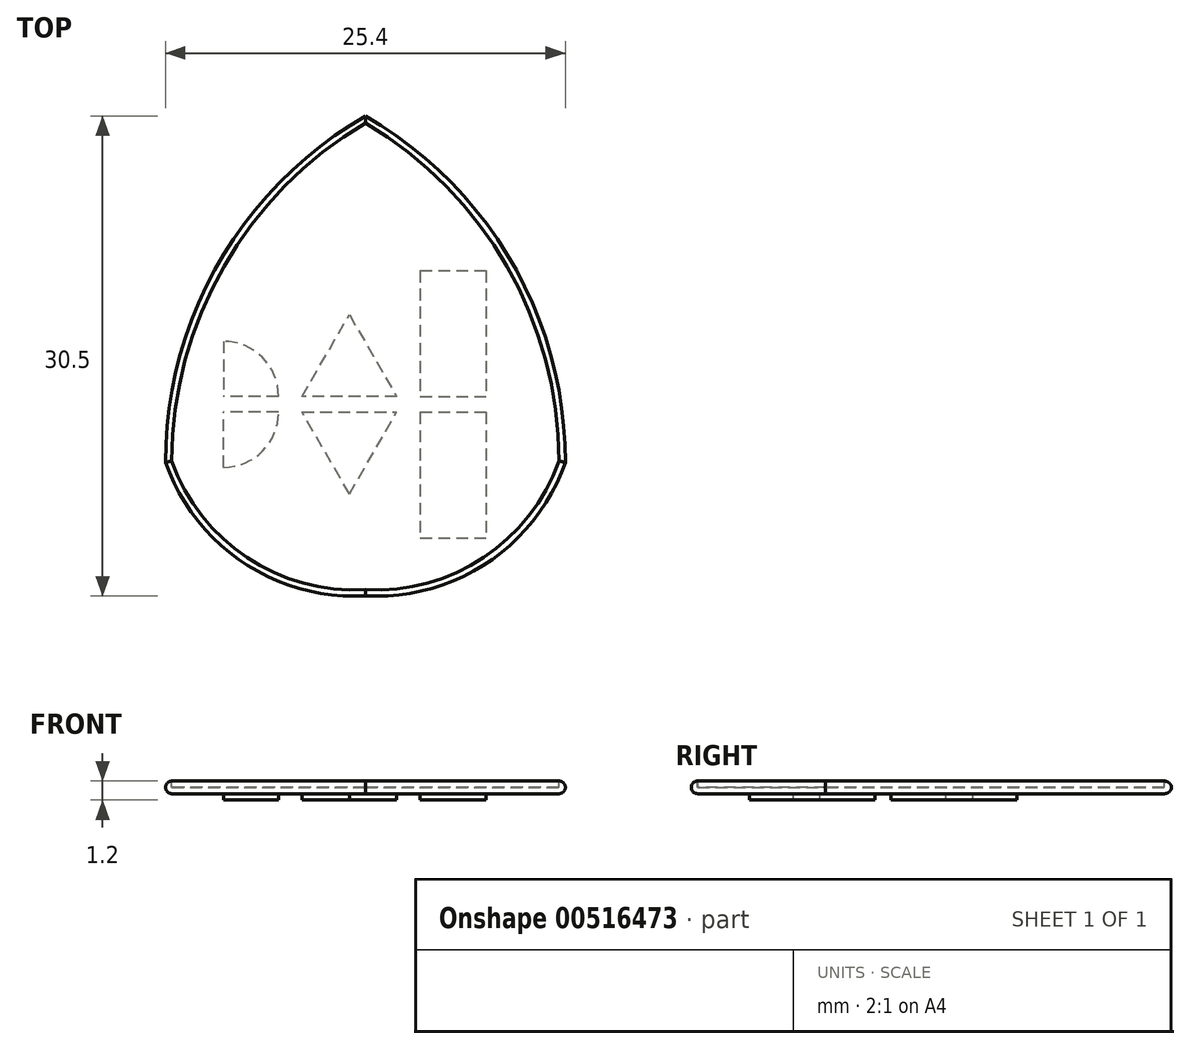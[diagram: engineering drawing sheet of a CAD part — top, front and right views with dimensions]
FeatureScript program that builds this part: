
annotation { "Feature Type Name" : "Feature", "Feature Type Description" : "" }
export const myFeature = defineFeature(function(context is Context, id is Id, definition is map)
    precondition{}
    {
        {
            var Q0;
            Q0=qCreatedBy(makeId("Top.planeOp"),FACE);
            var sketch = newSketch(context, id + "F0", { "sketchPlane" : qUnion([Q0])});
            skArc(sketch, "E0", {"start": v(-12.7, 16.18) * mm, "mid": v(-7.77, 9.82) * mm, "end": v(0, 7.7) * mm});
            skArc(sketch, "E1", {"start": v(0, 38.18) * mm, "mid": v(-9.3, 28.88) * mm, "end": v(-12.7, 16.18) * mm});
            skArc(sketch, "E2", {"start": v(0, 7.7) * mm, "mid": v(7.77, 9.82) * mm, "end": v(12.7, 16.18) * mm});
            skArc(sketch, "E3", {"start": v(12.7, 16.18) * mm, "mid": v(9.3, 28.88) * mm, "end": v(0, 38.18) * mm});
            skSolve(sketch);
        }
        {
            var Q0;
            Q0 = qSketchRegion(id + "F0", true);
            extrude(context, id + "F1", {"entities" : qUnion([Q0]), "depth" : 0.8 * mm, "offsetDistance" : 25.4 * mm});
        }
        {
            var Q0;
            Q0=makeQuery(id+"F1.opExtrude","CAP_EDGE",EDGE,{"disambiguationData":[OSD([sQuery(id+"F0.wireOp",EDGE,"E1")])],"isStart":false});
            var Q1;
            Q1=makeQuery(id+"F1.opExtrude","CAP_EDGE",EDGE,{"disambiguationData":[OSD([sQuery(id+"F0.wireOp",EDGE,"E0")])],"isStart":false});
            var Q2;
            Q2=makeQuery(id+"F1.opExtrude","CAP_EDGE",EDGE,{"disambiguationData":[OSD([sQuery(id+"F0.wireOp",EDGE,"E2")])],"isStart":false});
            var Q3;
            Q3=makeQuery(id+"F1.opExtrude","CAP_EDGE",EDGE,{"disambiguationData":[OSD([sQuery(id+"F0.wireOp",EDGE,"E3")])],"isStart":false});
            fillet(context, id + "F2", {"entities" : qUnion([Q0, Q1, Q2, Q3]), "radius" : 0.4 * mm, "tangentPropagation" : true, "allowEdgeOverflow" : false});
        }
        {
            var Q0;
            Q0=makeQuery(id+"F1.opExtrude","CAP_EDGE",EDGE,{"disambiguationData":[OSD([sQuery(id+"F0.wireOp",EDGE,"E2")])],"isStart":true});
            var Q1;
            Q1=makeQuery(id+"F1.opExtrude","CAP_EDGE",EDGE,{"disambiguationData":[OSD([sQuery(id+"F0.wireOp",EDGE,"E3")])],"isStart":true});
            var Q2;
            Q2=makeQuery(id+"F1.opExtrude","CAP_EDGE",EDGE,{"disambiguationData":[OSD([sQuery(id+"F0.wireOp",EDGE,"E0")])],"isStart":true});
            var Q3;
            Q3=makeQuery(id+"F1.opExtrude","CAP_EDGE",EDGE,{"disambiguationData":[OSD([sQuery(id+"F0.wireOp",EDGE,"E1")])],"isStart":true});
            fillet(context, id + "F3", {"entities" : qUnion([Q0, Q1, Q2, Q3]), "radius" : 0.4 * mm, "tangentPropagation" : true, "allowEdgeOverflow" : false});
        }
        {
            var Q0;
            Q0=qCreatedBy(makeId("Top.planeOp"),FACE);
            var sketch = newSketch(context, id + "F4", { "sketchPlane" : qUnion([Q0])});
            skArc(sketch, "E4", {"start": v(-9.02, 15.86) * mm, "mid": v(-6.54, 16.88) * mm, "end": v(-5.52, 19.36) * mm});
            skLineSegment(sketch, "E5", {"start": v(-9.02, 15.86) * mm, "end": v(-9.02, 19.36) * mm});
            skLineSegment(sketch, "E6", {"start": v(-5.52, 19.36) * mm, "end": v(-9.02, 19.36) * mm});
            skArc(sketch, "E7", {"start": v(-5.52, 20.36) * mm, "mid": v(-6.54, 22.83) * mm, "end": v(-9.02, 23.86) * mm});
            skLineSegment(sketch, "E8", {"start": v(-9.02, 23.86) * mm, "end": v(-9.02, 20.36) * mm});
            skLineSegment(sketch, "E9", {"start": v(-5.52, 20.36) * mm, "end": v(-9.02, 20.36) * mm});
            skLineSegment(sketch, "E10", {"start": v(-4.02, 20.36) * mm, "end": v(-1.02, 25.55) * mm});
            skLineSegment(sketch, "E11", {"start": v(-1.02, 25.55) * mm, "end": v(1.98, 20.36) * mm});
            skLineSegment(sketch, "E12", {"start": v(1.98, 20.36) * mm, "end": v(-4.02, 20.36) * mm});
            skLineSegment(sketch, "E13", {"start": v(-4.02, 19.36) * mm, "end": v(1.98, 19.36) * mm});
            skLineSegment(sketch, "E14", {"start": v(-1.02, 14.16) * mm, "end": v(-4.02, 19.36) * mm});
            skLineSegment(sketch, "E15.bottom", {"start": v(3.48, 28.36) * mm, "end": v(7.65, 28.36) * mm});
            skLineSegment(sketch, "E15.top", {"start": v(3.48, 20.36) * mm, "end": v(7.65, 20.36) * mm});
            skLineSegment(sketch, "E15.left", {"start": v(3.48, 28.36) * mm, "end": v(3.48, 20.36) * mm});
            skLineSegment(sketch, "E15.right", {"start": v(7.65, 28.36) * mm, "end": v(7.65, 20.36) * mm});
            skLineSegment(sketch, "E16.bottom", {"start": v(3.48, 19.36) * mm, "end": v(7.65, 19.36) * mm});
            skLineSegment(sketch, "E16.top", {"start": v(3.48, 11.36) * mm, "end": v(7.65, 11.36) * mm});
            skLineSegment(sketch, "E16.left", {"start": v(3.48, 19.36) * mm, "end": v(3.48, 11.36) * mm});
            skLineSegment(sketch, "E16.right", {"start": v(7.65, 19.36) * mm, "end": v(7.65, 11.36) * mm});
            skLineSegment(sketch, "E17", {"start": v(-1.02, 14.16) * mm, "end": v(1.98, 19.36) * mm});
            skSolve(sketch);
        }
        {
            var Q0;
            Q0=makeQuery(id+"F4.imprint","IMPRINT",FACE,{"disambiguationData":[TD([[makeQuery(id+"F4.imprint","IMPRINT",EDGE,{"derivedFrom":sQuery(id+"F4.wireOp",EDGE,"E13")}),-1.0]])]});
            var Q1;
            Q1=makeQuery(id+"F4.imprint","IMPRINT",FACE,{"disambiguationData":[TD([[makeQuery(id+"F4.imprint","IMPRINT",EDGE,{"derivedFrom":sQuery(id+"F4.wireOp",EDGE,"E4")}),1.0]])]});
            var Q2;
            Q2=makeQuery(id+"F4.imprint","IMPRINT",FACE,{"disambiguationData":[TD([[makeQuery(id+"F4.imprint","IMPRINT",EDGE,{"derivedFrom":sQuery(id+"F4.wireOp",EDGE,"E10")}),-1.0]])]});
            var Q3;
            Q3=makeQuery(id+"F4.imprint","IMPRINT",FACE,{"disambiguationData":[TD([[makeQuery(id+"F4.imprint","IMPRINT",EDGE,{"derivedFrom":sQuery(id+"F4.wireOp",EDGE,"E16.bottom")}),-1.0]])]});
            var Q4;
            Q4=makeQuery(id+"F4.imprint","IMPRINT",FACE,{"disambiguationData":[TD([[makeQuery(id+"F4.imprint","IMPRINT",EDGE,{"derivedFrom":sQuery(id+"F4.wireOp",EDGE,"E7")}),1.0]])]});
            var Q5;
            Q5=makeQuery(id+"F4.imprint","IMPRINT",FACE,{"disambiguationData":[TD([[makeQuery(id+"F4.imprint","IMPRINT",EDGE,{"derivedFrom":sQuery(id+"F4.wireOp",EDGE,"E15.bottom")}),-1.0]])]});
            var Q6;
            Q6=makeQuery(id+"F1.opExtrude","CAP_FACE",FACE,{"disambiguationData":[OSD([sQuery(id+"F0.wireOp",EDGE,"E0"),sQuery(id+"F0.wireOp",EDGE,"E1"),sQuery(id+"F0.wireOp",EDGE,"E2"),sQuery(id+"F0.wireOp",EDGE,"E3")])],"isStart":false});
            var Q7;
            Q7=makeQuery(id+"F1.opExtrude","CAP_FACE",FACE,{"disambiguationData":[OSD([sQuery(id+"F0.wireOp",EDGE,"E0"),sQuery(id+"F0.wireOp",EDGE,"E1"),sQuery(id+"F0.wireOp",EDGE,"E2"),sQuery(id+"F0.wireOp",EDGE,"E3")])],"isStart":true});
            var Q8;
            Q8=sQuery(id+"F4.wireOp",EDGE,"E16.top");
            var Q9;
            Q9=sQuery(id+"F4.wireOp",EDGE,"E15.top");
            var Q10;
            Q10=sQuery(id+"F4.wireOp",EDGE,"E15.bottom");
            var Q11;
            Q11=sQuery(id+"F4.wireOp",EDGE,"E16.bottom");
            var Q12;
            Q12=sQuery(id+"F4.wireOp",EDGE,"E15.right");
            var Q13;
            Q13=sQuery(id+"F4.wireOp",EDGE,"E15.left");
            var Q14;
            Q14=sQuery(id+"F4.wireOp",EDGE,"E16.right");
            var Q15;
            Q15=sQuery(id+"F4.wireOp",EDGE,"E16.left");
            var Q16;
            Q16=sQuery(id+"F4.wireOp",EDGE,"E11");
            var Q17;
            Q17=sQuery(id+"F4.wireOp",EDGE,"E14");
            var Q18;
            Q18=sQuery(id+"F4.wireOp",EDGE,"E12");
            var Q19;
            Q19=sQuery(id+"F4.wireOp",EDGE,"E7");
            var Q20;
            Q20=sQuery(id+"F4.wireOp",EDGE,"E17");
            var Q21;
            Q21=sQuery(id+"F4.wireOp",EDGE,"E4");
            var Q22;
            Q22=sQuery(id+"F4.wireOp",EDGE,"E10");
            var Q23;
            Q23=sQuery(id+"F4.wireOp",EDGE,"E13");
            var Q24;
            Q24=sQuery(id+"F4.wireOp",EDGE,"E8");
            var Q25;
            Q25=sQuery(id+"F4.wireOp",EDGE,"E6");
            var Q26;
            Q26=sQuery(id+"F4.wireOp",EDGE,"E9");
            var Q27;
            Q27=sQuery(id+"F4.wireOp",EDGE,"E5");
            extrude(context, id + "F5", {"entities" : qUnion([Q0, Q1, Q2, Q3, Q4, Q5, Q6, Q7]), "operationType" : NewBodyOperationType.REMOVE, "surfaceEntities" : qUnion([Q8, Q9, Q10, Q11, Q12, Q13, Q14, Q15, Q16, Q17, Q18, Q19, Q20, Q21, Q22, Q23, Q24, Q25, Q26, Q27]), "oppositeDirection" : true, "depth" : 0.4 * mm, "offsetDistance" : 25 * mm});
        }
        {
            var Q0;
            Q0 = qSketchRegion(id + "F4", true);
            extrude(context, id + "F6", {"entities" : qUnion([Q0]), "operationType" : NewBodyOperationType.ADD, "oppositeDirection" : true, "depth" : 0.4 * mm, "offsetDistance" : 25 * mm});
        }
    });
